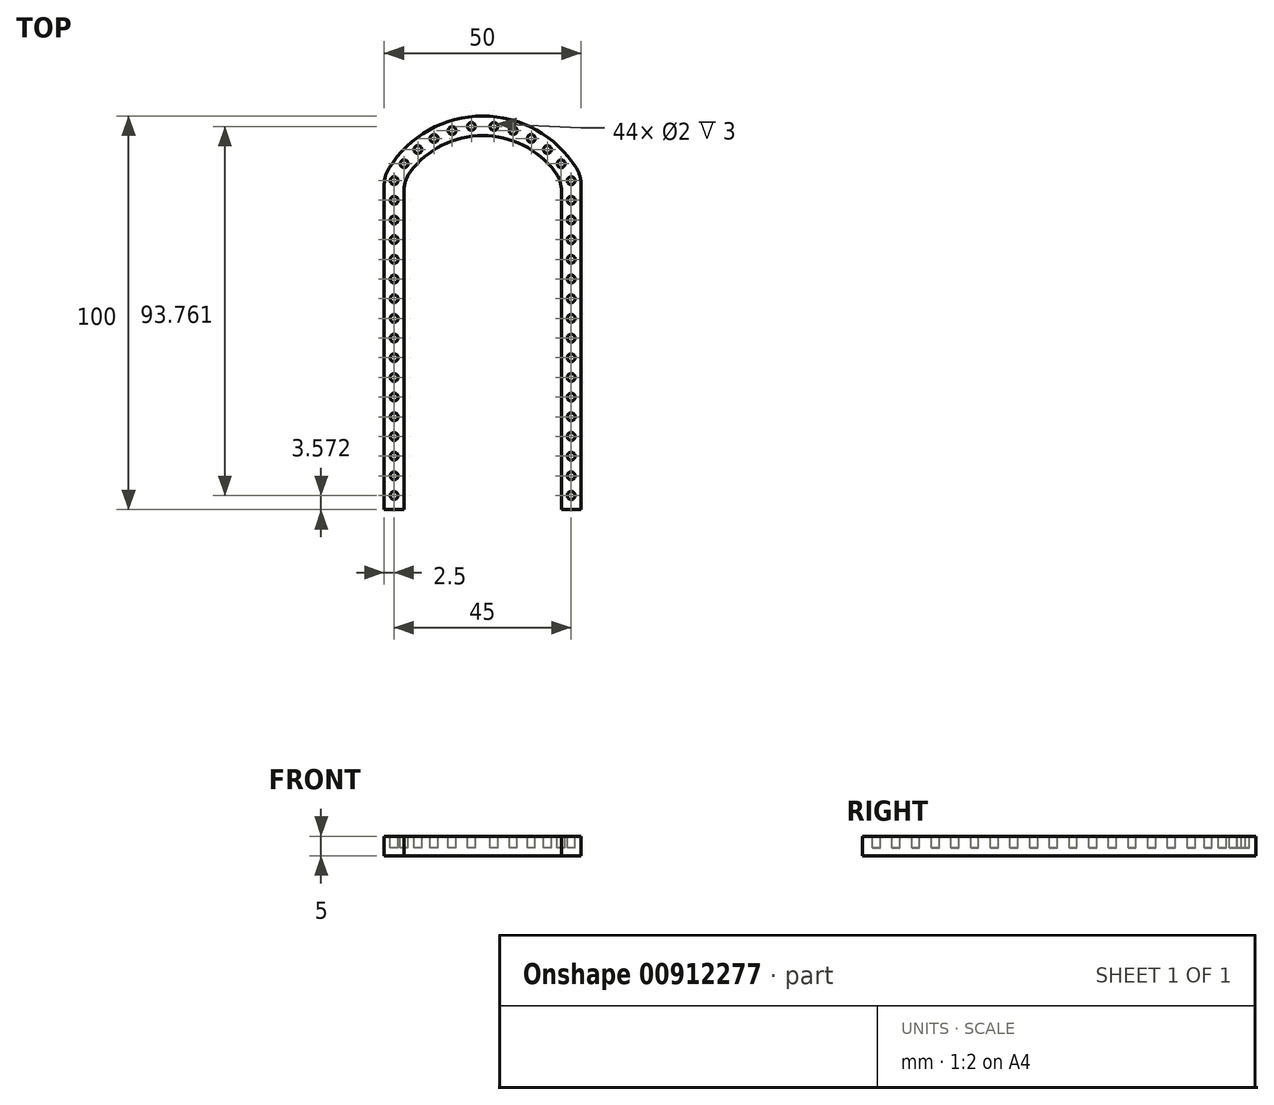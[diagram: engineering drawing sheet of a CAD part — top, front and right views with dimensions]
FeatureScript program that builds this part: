
annotation { "Feature Type Name" : "Feature", "Feature Type Description" : "" }
export const myFeature = defineFeature(function(context is Context, id is Id, definition is map)
    precondition{}
    {
        {
            var Q0;
            Q0=qCreatedBy(makeId("Top.planeOp"),FACE);
            var sketch = newSketch(context, id + "F0", { "sketchPlane" : qUnion([Q0])});
            skLineSegment(sketch, "E0", {"start": v(-25, 22.5) * mm, "end": v(-25, -62.07) * mm});
            skLineSegment(sketch, "E1.MirrorCS", {"start": v(25, 22.5) * mm, "end": v(25, -62.07) * mm});
            skArc(sketch, "E2", {"start": v(25, 22.5) * mm, "mid": v(0, 37.93) * mm, "end": v(-25, 22.5) * mm});
            skLineSegment(sketch, "E3.0", {"start": v(-20, 21.26) * mm, "end": v(-20, -62.07) * mm});
            skArc(sketch, "E3.1", {"start": v(20, 21.26) * mm, "mid": v(0, 32.93) * mm, "end": v(-20, 21.26) * mm});
            skLineSegment(sketch, "E3.2", {"start": v(20, 21.26) * mm, "end": v(20, -62.07) * mm});
            skLineSegment(sketch, "E4", {"start": v(-25, -62.07) * mm, "end": v(-20, -62.07) * mm});
            skLineSegment(sketch, "E5", {"start": v(20, -62.07) * mm, "end": v(25, -62.07) * mm});
            skPoint(sketch, "E6", {"position": v(0, 37.93) * mm});
            skSolve(sketch);
        }
        {
            var Q0;
            Q0 = qSketchRegion(id + "F0", true);
            extrude(context, id + "F1", {"entities" : qUnion([Q0]), "depth" : 5 * mm, "offsetDistance" : 25 * mm});
        }
        {
            var Q0;
            Q0=makeQuery(id+"F1.opExtrude","CAP_FACE",FACE,{"disambiguationData":[OSD([sQuery(id+"F0.wireOp",EDGE,"E0"),sQuery(id+"F0.wireOp",EDGE,"E1.MirrorCS"),sQuery(id+"F0.wireOp",EDGE,"E2"),sQuery(id+"F0.wireOp",EDGE,"E3.0"),sQuery(id+"F0.wireOp",EDGE,"E3.1"),sQuery(id+"F0.wireOp",EDGE,"E3.2"),sQuery(id+"F0.wireOp",EDGE,"E4"),sQuery(id+"F0.wireOp",EDGE,"E5")])],"isStart":false});
            var sketch = newSketch(context, id + "F2", { "sketchPlane" : qUnion([Q0])});
            skCircle(sketch, "E7", {"center": v(-22.5, -13.5) * mm, "radius": 1 * mm});
            skPoint(sketch, "E7.centerSnap0", {"position": v(-22.5, -62.07) * mm});
            skCircle(sketch, "E8", {"center": v(-22.5, -8.5) * mm, "radius": 1 * mm});
            skCircle(sketch, "E9", {"center": v(-22.5, -3.5) * mm, "radius": 1 * mm});
            skCircle(sketch, "E10", {"center": v(-22.5, 1.5) * mm, "radius": 1 * mm});
            skCircle(sketch, "E11", {"center": v(-22.5, 6.5) * mm, "radius": 1 * mm});
            skCircle(sketch, "E12", {"center": v(-22.5, 11.5) * mm, "radius": 1 * mm});
            skCircle(sketch, "E13", {"center": v(-22.5, 16.5) * mm, "radius": 1 * mm});
            skCircle(sketch, "E14", {"center": v(-22.5, 21.5) * mm, "radius": 1 * mm});
            skCircle(sketch, "E15", {"center": v(-19.94, 25.8) * mm, "radius": 1 * mm});
            skCircle(sketch, "E16", {"center": v(-16.46, 29.39) * mm, "radius": 1 * mm});
            skCircle(sketch, "E17", {"center": v(-12.35, 32.23) * mm, "radius": 1 * mm});
            skCircle(sketch, "E18", {"center": v(-7.76, 34.21) * mm, "radius": 1 * mm});
            skCircle(sketch, "E19", {"center": v(-2.87, 35.26) * mm, "radius": 1 * mm});
            skCircle(sketch, "E20.MirrorC", {"center": v(2.87, 35.26) * mm, "radius": 1 * mm});
            skCircle(sketch, "E21.MirrorC", {"center": v(7.76, 34.21) * mm, "radius": 1 * mm});
            skCircle(sketch, "E22.MirrorC", {"center": v(12.35, 32.23) * mm, "radius": 1 * mm});
            skCircle(sketch, "E23.MirrorC", {"center": v(16.46, 29.39) * mm, "radius": 1 * mm});
            skCircle(sketch, "E24.MirrorC", {"center": v(19.94, 25.8) * mm, "radius": 1 * mm});
            skCircle(sketch, "E25.MirrorC", {"center": v(22.5, 21.5) * mm, "radius": 1 * mm});
            skCircle(sketch, "E26.MirrorC", {"center": v(22.5, 16.5) * mm, "radius": 1 * mm});
            skCircle(sketch, "E27.MirrorC", {"center": v(22.5, 11.5) * mm, "radius": 1 * mm});
            skCircle(sketch, "E28.MirrorC", {"center": v(22.5, 6.5) * mm, "radius": 1 * mm});
            skCircle(sketch, "E29.MirrorC", {"center": v(22.5, 1.5) * mm, "radius": 1 * mm});
            skCircle(sketch, "E30.MirrorC", {"center": v(22.5, -3.5) * mm, "radius": 1 * mm});
            skCircle(sketch, "E31.MirrorC", {"center": v(22.5, -8.5) * mm, "radius": 1 * mm});
            skCircle(sketch, "E32.MirrorC", {"center": v(22.5, -13.5) * mm, "radius": 1 * mm});
            skLineSegment(sketch, "E33", {"start": v(-41.98, -16) * mm, "end": v(44.48, -16) * mm, "construction": true});
            skPoint(sketch, "E33.startSnap0", {"position": v(-25, -16) * mm});
            skCircle(sketch, "E34.MirrorC", {"center": v(22.5, -18.5) * mm, "radius": 1 * mm});
            skCircle(sketch, "E35.MirrorC", {"center": v(22.5, -23.5) * mm, "radius": 1 * mm});
            skCircle(sketch, "E36.MirrorC", {"center": v(22.5, -28.5) * mm, "radius": 1 * mm});
            skCircle(sketch, "E37.MirrorC", {"center": v(22.5, -33.5) * mm, "radius": 1 * mm});
            skCircle(sketch, "E38.MirrorC", {"center": v(22.5, -48.5) * mm, "radius": 1 * mm});
            skCircle(sketch, "E39.MirrorC", {"center": v(22.5, -38.5) * mm, "radius": 1 * mm});
            skCircle(sketch, "E40.MirrorC", {"center": v(22.5, -43.5) * mm, "radius": 1 * mm});
            skCircle(sketch, "E41.MirrorC", {"center": v(22.5, -53.5) * mm, "radius": 1 * mm});
            skCircle(sketch, "E42.MirrorC", {"center": v(-22.5, -18.5) * mm, "radius": 1 * mm});
            skCircle(sketch, "E43.MirrorC", {"center": v(-22.5, -23.5) * mm, "radius": 1 * mm});
            skCircle(sketch, "E44.MirrorC", {"center": v(-22.5, -28.5) * mm, "radius": 1 * mm});
            skCircle(sketch, "E45.MirrorC", {"center": v(-22.5, -33.5) * mm, "radius": 1 * mm});
            skCircle(sketch, "E46.MirrorC", {"center": v(-22.5, -38.5) * mm, "radius": 1 * mm});
            skCircle(sketch, "E47.MirrorC", {"center": v(-22.5, -43.5) * mm, "radius": 1 * mm});
            skCircle(sketch, "E48.MirrorC", {"center": v(-22.5, -48.5) * mm, "radius": 1 * mm});
            skCircle(sketch, "E49.MirrorC", {"center": v(-22.5, -53.5) * mm, "radius": 1 * mm});
            skCircle(sketch, "E50", {"center": v(-22.5, -58.5) * mm, "radius": 1 * mm});
            skCircle(sketch, "E51.MirrorC", {"center": v(22.5, -58.5) * mm, "radius": 1 * mm});
            skSolve(sketch);
        }
        {
            var Q0;
            Q0 = qSketchRegion(id + "F2", true);
            extrude(context, id + "F3", {"entities" : qUnion([Q0]), "operationType" : NewBodyOperationType.REMOVE, "oppositeDirection" : true, "depth" : 3 * mm, "offsetDistance" : 25 * mm});
        }
        {
            var Q0;
            Q0=makeQuery(id+"F1.opExtrude","SWEPT_EDGE",EDGE,{"disambiguationData":[OSD([sQuery(id+"F0.wireOp",EDGE,"E0"),sQuery(id+"F0.wireOp",EDGE,"E2")])]});
            var Q1;
            Q1=makeQuery(id+"F1.opExtrude","SWEPT_EDGE",EDGE,{"disambiguationData":[OSD([sQuery(id+"F0.wireOp",EDGE,"E3.0"),sQuery(id+"F0.wireOp",EDGE,"E3.1")])]});
            var Q2;
            Q2=makeQuery(id+"F1.opExtrude","SWEPT_EDGE",EDGE,{"disambiguationData":[OSD([sQuery(id+"F0.wireOp",EDGE,"E1.MirrorCS"),sQuery(id+"F0.wireOp",EDGE,"E2")])]});
            var Q3;
            Q3=makeQuery(id+"F1.opExtrude","SWEPT_EDGE",EDGE,{"disambiguationData":[OSD([sQuery(id+"F0.wireOp",EDGE,"E3.1"),sQuery(id+"F0.wireOp",EDGE,"E3.2")])]});
            fillet(context, id + "F4", {"entities" : qUnion([Q0, Q1, Q2, Q3]), "radius" : 8 * mm, "tangentPropagation" : true, "allowEdgeOverflow" : false});
        }
    });
